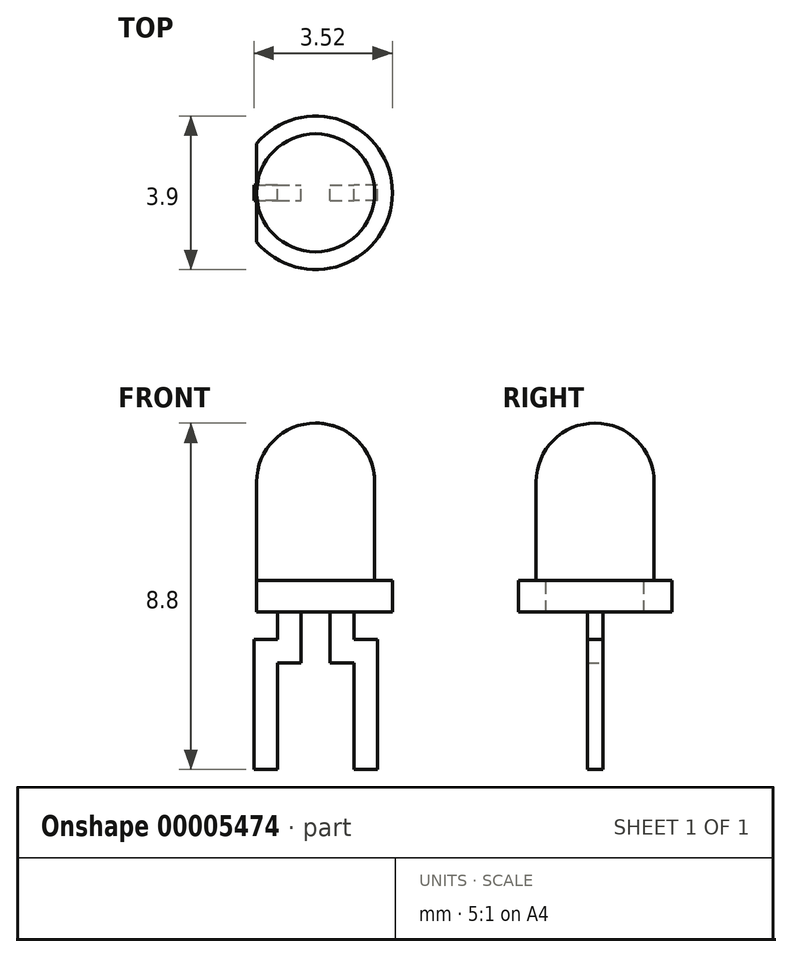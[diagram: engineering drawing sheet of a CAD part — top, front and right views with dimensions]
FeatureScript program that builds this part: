
annotation { "Feature Type Name" : "Feature", "Feature Type Description" : "" }
export const myFeature = defineFeature(function(context is Context, id is Id, definition is map)
    precondition{}
    {
        {
            var Q0;
            Q0=qCreatedBy(makeId("Front.planeOp"),FACE);
            var sketch = newSketch(context, id + "F0", { "sketchPlane" : qUnion([Q0])});
            skArc(sketch, "E0", {"start": v(0, 0) * mm, "mid": v(-1.06, -0.44) * mm, "end": v(-1.5, -1.5) * mm});
            skLineSegment(sketch, "E1", {"start": v(-1.5, -1.5) * mm, "end": v(-1.5, -4) * mm});
            skLineSegment(sketch, "E2", {"start": v(-1.5, -4) * mm, "end": v(-1.95, -4) * mm});
            skLineSegment(sketch, "E3", {"start": v(-1.95, -4) * mm, "end": v(-1.95, -4.8) * mm});
            skLineSegment(sketch, "E4", {"start": v(-1.95, -4.8) * mm, "end": v(0, -4.8) * mm});
            skLineSegment(sketch, "E5", {"start": v(0, 0) * mm, "end": v(0, -4.8) * mm});
            skLineSegment(sketch, "E6", {"start": v(-0.97, -4.8) * mm, "end": v(-0.97, -5.5) * mm});
            skLineSegment(sketch, "E7", {"start": v(-0.97, -5.5) * mm, "end": v(-1.57, -5.5) * mm});
            skLineSegment(sketch, "E8", {"start": v(-1.57, -5.5) * mm, "end": v(-1.57, -8.8) * mm});
            skLineSegment(sketch, "E9", {"start": v(-1.57, -8.8) * mm, "end": v(-0.97, -8.8) * mm});
            skLineSegment(sketch, "E10", {"start": v(-0.97, -8.8) * mm, "end": v(-0.97, -6.1) * mm});
            skLineSegment(sketch, "E11", {"start": v(-0.97, -6.1) * mm, "end": v(-0.37, -6.1) * mm});
            skLineSegment(sketch, "E12", {"start": v(-0.37, -6.1) * mm, "end": v(-0.37, -4.8) * mm});
            skPoint(sketch, "E13", {"position": v(-1.27, -8.8) * mm});
            skLineSegment(sketch, "E14.0.MirrorCS", {"start": v(0.97, -4.8) * mm, "end": v(0.97, -5.5) * mm});
            skLineSegment(sketch, "E14.1.MirrorCS", {"start": v(0.37, -6.1) * mm, "end": v(0.37, -4.8) * mm});
            skLineSegment(sketch, "E14.2.MirrorCS", {"start": v(0.97, -6.1) * mm, "end": v(0.37, -6.1) * mm});
            skLineSegment(sketch, "E14.3.MirrorCS", {"start": v(0.97, -5.5) * mm, "end": v(1.57, -5.5) * mm});
            skLineSegment(sketch, "E14.4.MirrorCS", {"start": v(0.97, -8.8) * mm, "end": v(0.97, -6.1) * mm});
            skLineSegment(sketch, "E14.5.MirrorCS", {"start": v(1.57, -5.5) * mm, "end": v(1.57, -8.8) * mm});
            skLineSegment(sketch, "E14.6.MirrorCS", {"start": v(1.57, -8.8) * mm, "end": v(0.97, -8.8) * mm});
            skLineSegment(sketch, "E15", {"start": v(0.37, -4.8) * mm, "end": v(0.97, -4.8) * mm});
            skLineSegment(sketch, "E16", {"start": v(-1.5, -4.8) * mm, "end": v(-1.5, -4) * mm});
            skSolve(sketch);
        }
        {
            var Q0;
            Q0=makeQuery(id+"F0.imprint","IMPRINT",FACE,{"disambiguationData":[TD([[makeQuery(id+"F0.imprint","IMPRINT",EDGE,{"derivedFrom":sQuery(id+"F0.wireOp",EDGE,"E0")}),1.0]])]});
            var Q1;
            {var subQ2=sQuery(id+"F0.wireOp",EDGE,"E3");Q1=makeQuery(id+"F0.imprint","IMPRINT",FACE,{"disambiguationData":[TD([[makeQuery(id+"F0.imprint","IMPRINT",EDGE,{"derivedFrom":subQ2}),1.0]])]});}
            var Q2;
            Q2=sQuery(id+"F0.wireOp",EDGE,"E5");
            revolve(context, id + "F1", {"entities" : qUnion([Q0, Q1]), "axis" : qUnion([Q2]), "revolveType" : RevolveType.FULL});
        }
        {
            var Q0;
            {var subQ2=sQuery(id+"F0.wireOp",EDGE,"E3");Q0=makeQuery(id+"F0.imprint","IMPRINT",FACE,{"disambiguationData":[TD([[makeQuery(id+"F0.imprint","IMPRINT",EDGE,{"derivedFrom":subQ2}),1.0]])]});}
            var Q1;
            Q1=makeQuery(id+"F0.imprint","IMPRINT",FACE,{"disambiguationData":[TD([[makeQuery(id+"F0.imprint","IMPRINT",EDGE,{"derivedFrom":sQuery(id+"F0.wireOp",EDGE,"40c9677c-bd0f-4d02-a515-d1e38aefdd19.0.MirrorCS")}),-1.0]])]});
            extrude(context, id + "F2", {"entities" : qUnion([Q0, Q1]), "operationType" : NewBodyOperationType.REMOVE, "endBound" : BoundingType.THROUGH_ALL, "oppositeDirection" : true, "depth" : 25 * mm, "hasSecondDirection" : true, "secondDirectionBound" : BoundingType.THROUGH_ALL, "secondDirectionOppositeDirection" : false, "secondDirectionDepth" : 25 * mm});
        }
        {
            var Q0;
            Q0=makeQuery(id+"F0.imprint","IMPRINT",FACE,{"disambiguationData":[TD([[makeQuery(id+"F0.imprint","IMPRINT",EDGE,{"derivedFrom":sQuery(id+"F0.wireOp",EDGE,"E14.0.MirrorCS")}),-1.0]])]});
            var Q1;
            {var subQ1=sQuery(id+"F0.wireOp",EDGE,"E6");Q1=makeQuery(id+"F0.imprint","IMPRINT",FACE,{"disambiguationData":[TD([[makeQuery(id+"F0.imprint","IMPRINT",EDGE,{"derivedFrom":subQ1}),1.0]])]});}
            extrude(context, id + "F3", {"entities" : qUnion([Q0, Q1]), "operationType" : NewBodyOperationType.ADD, "depth" : .4 * mm, "symmetric" : true});
        }
    });
